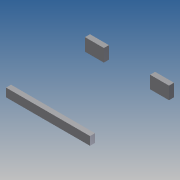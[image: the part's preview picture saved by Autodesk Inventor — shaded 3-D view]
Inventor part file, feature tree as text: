
AUTODESK INVENTOR PART (.ipt)
format: ipt  version: 2014 (Build 180170000, 170)  size: 129,024 bytes
history: native  units: mm
features: extrude x2
ambient origin geometry x8: Origin, YZ Plane, XZ Plane, XY Plane, X Axis, Y Axis, Z Axis, Center Point
bodies: Body1 (feature_tree)
feature tree (2):
  extrude  "Extrusion5"  Depth=1000.0mm
  extrude  "Extrusion6"  Depth=1000.0mm
